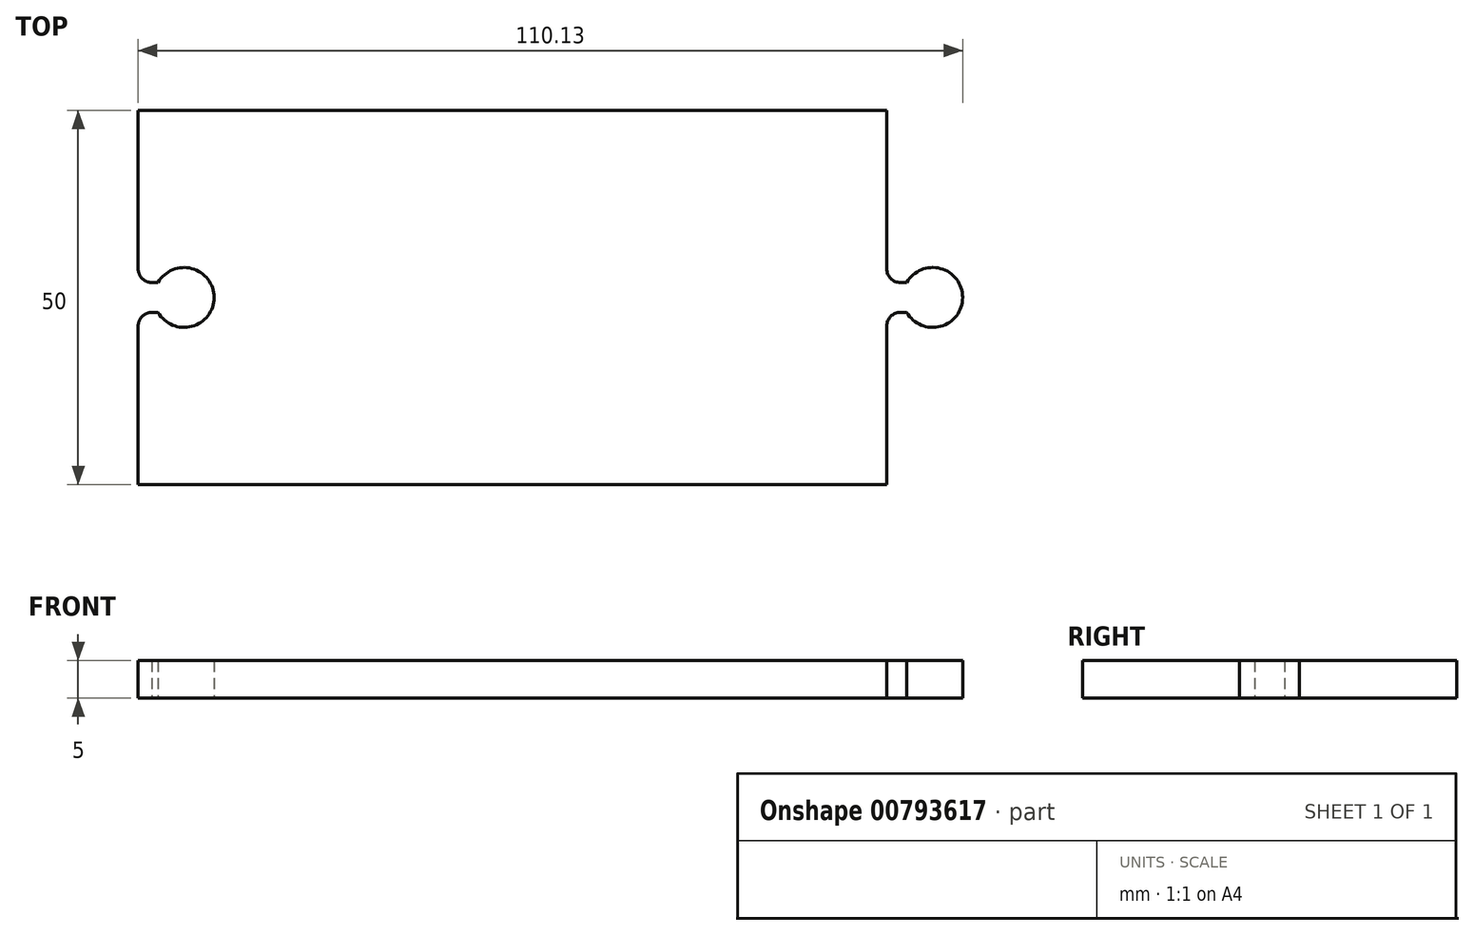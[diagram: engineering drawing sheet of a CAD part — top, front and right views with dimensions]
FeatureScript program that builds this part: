
annotation { "Feature Type Name" : "Feature", "Feature Type Description" : "" }
export const myFeature = defineFeature(function(context is Context, id is Id, definition is map)
    precondition{}
    {
        {
            var Q0;
            Q0=qCreatedBy(makeId("Top.planeOp"),FACE);
            var sketch = newSketch(context, id + "F0", { "sketchPlane" : qUnion([Q0])});
            skLineSegment(sketch, "E0", {"start": v(-59.76, 38.41) * mm, "end": v(-59.76, 19.41) * mm});
            skLineSegment(sketch, "E1", {"start": v(-59.76, 38.41) * mm, "end": v(-9.76, 38.41) * mm});
            skLineSegment(sketch, "E2", {"start": v(-59.76, 7.41) * mm, "end": v(-59.76, -11.59) * mm});
            skLineSegment(sketch, "E3", {"start": v(-59.76, -11.59) * mm, "end": v(-9.76, -11.59) * mm});
            skPoint(sketch, "E4.visualSharp", {"position": v(-59.76, 15.41) * mm});
            skPoint(sketch, "E5.visualSharp", {"position": v(-59.76, 11.41) * mm});
            skPoint(sketch, "E6.start.orphan", {"position": v(-49.3, 15.41) * mm});
            skLineSegment(sketch, "E7", {"start": v(-9.76, 38.41) * mm, "end": v(-9.76, 19.41) * mm});
            skLineSegment(sketch, "E8", {"start": v(-9.76, 7.41) * mm, "end": v(-9.76, -11.59) * mm});
            skPoint(sketch, "E9.visualSharp", {"position": v(-9.76, 15.41) * mm});
            skPoint(sketch, "E10.visualSharp", {"position": v(-9.76, 11.41) * mm});
            skPoint(sketch, "E11.start.orphan", {"position": v(0.7, 15.41) * mm});
            skLineSegment(sketch, "E12", {"start": v(-59.76, 7.41) * mm, "end": v(-59.76, 9.61) * mm});
            skPoint(sketch, "E5.filletArc.start.orphan", {"position": v(-55.76, 11.41) * mm});
            skArc(sketch, "E13.filletArc", {"start": v(-57.95, 11.41) * mm, "mid": v(-59.23, 10.88) * mm, "end": v(-59.76, 9.61) * mm});
            skPoint(sketch, "E4.filletArc.end.orphan", {"position": v(-55.76, 15.41) * mm});
            skLineSegment(sketch, "E14", {"start": v(-59.76, 19.41) * mm, "end": v(-59.76, 17.22) * mm});
            skArc(sketch, "E15.filletArc", {"start": v(-59.76, 17.22) * mm, "mid": v(-59.23, 15.94) * mm, "end": v(-57.95, 15.42) * mm});
            skPoint(sketch, "E10.filletArc.start.orphan", {"position": v(-5.76, 11.41) * mm});
            skLineSegment(sketch, "E16", {"start": v(-9.76, 19.41) * mm, "end": v(-9.76, 17.22) * mm});
            skLineSegment(sketch, "E17", {"start": v(-9.76, 7.41) * mm, "end": v(-9.76, 9.61) * mm});
            skArc(sketch, "E18.filletArc", {"start": v(-9.76, 17.22) * mm, "mid": v(-9.23, 15.94) * mm, "end": v(-7.95, 15.42) * mm});
            skArc(sketch, "E19.filletArc", {"start": v(-7.95, 11.41) * mm, "mid": v(-9.23, 10.88) * mm, "end": v(-9.76, 9.61) * mm});
            skLineSegment(sketch, "E20", {"start": v(-9.76, 38.41) * mm, "end": v(40.24, 38.41) * mm});
            skLineSegment(sketch, "E21", {"start": v(40.24, -11.59) * mm, "end": v(-9.76, -11.59) * mm});
            skLineSegment(sketch, "E22", {"start": v(40.24, 38.41) * mm, "end": v(40.24, 17.21) * mm});
            skLineSegment(sketch, "E23", {"start": v(40.24, -11.59) * mm, "end": v(40.24, 9.61) * mm});
            skLineSegment(sketch, "E24", {"start": v(42.04, 11.41) * mm, "end": v(42.9, 11.41) * mm});
            skPoint(sketch, "E25.visualSharp", {"position": v(40.24, 15.41) * mm});
            skArc(sketch, "E25.filletArc", {"start": v(40.24, 17.21) * mm, "mid": v(40.77, 15.94) * mm, "end": v(42.04, 15.41) * mm});
            skPoint(sketch, "E26.visualSharp", {"position": v(40.24, 11.41) * mm});
            skArc(sketch, "E26.filletArc", {"start": v(42.04, 11.41) * mm, "mid": v(40.77, 10.89) * mm, "end": v(40.24, 9.61) * mm});
            skArc(sketch, "E27", {"start": v(42.9, 11.41) * mm, "mid": v(50.37, 13.41) * mm, "end": v(42.9, 15.41) * mm});
            skLineSegment(sketch, "E28.trimOffspring", {"start": v(42.9, 15.41) * mm, "end": v(42.04, 15.41) * mm});
            skPoint(sketch, "E29.end.orphan", {"position": v(50.7, 15.41) * mm});
            skPoint(sketch, "E30.trimOffspring.end.orphan", {"position": v(50.7, 11.41) * mm});
            skPoint(sketch, "E31.center.orphan", {"position": v(-2.53, 13.41) * mm});
            skLineSegment(sketch, "E32", {"start": v(-7.95, 11.41) * mm, "end": v(-7.09, 11.41) * mm});
            skLineSegment(sketch, "E33", {"start": v(-7.95, 15.42) * mm, "end": v(-7.09, 15.42) * mm});
            skLineSegment(sketch, "E34", {"start": v(-7.95, 11.41) * mm, "end": v(-7.95, 11.41) * mm});
            skArc(sketch, "E35", {"start": v(-7.09, 11.41) * mm, "mid": v(0.38, 13.41) * mm, "end": v(-7.09, 15.42) * mm});
            skPoint(sketch, "E36.center.orphan", {"position": v(-52.53, 13.41) * mm});
            skLineSegment(sketch, "E37", {"start": v(-57.95, 11.41) * mm, "end": v(-57.09, 11.41) * mm});
            skLineSegment(sketch, "E38", {"start": v(-57.95, 15.42) * mm, "end": v(-57.09, 15.42) * mm});
            skArc(sketch, "E39", {"start": v(-57.09, 11.41) * mm, "mid": v(-49.62, 13.41) * mm, "end": v(-57.09, 15.42) * mm});
            skLineSegment(sketch, "E40.trimOffspring", {"start": v(-57.95, 11.41) * mm, "end": v(-57.95, 11.41) * mm});
            skSolve(sketch);
        }
        {
            var Q0;
            Q0 = qSketchRegion(id + "F0", true);
            extrude(context, id + "F1", {"entities" : qUnion([Q0]), "depth" : 5 * mm, "offsetDistance" : 25 * mm});
        }
    });
